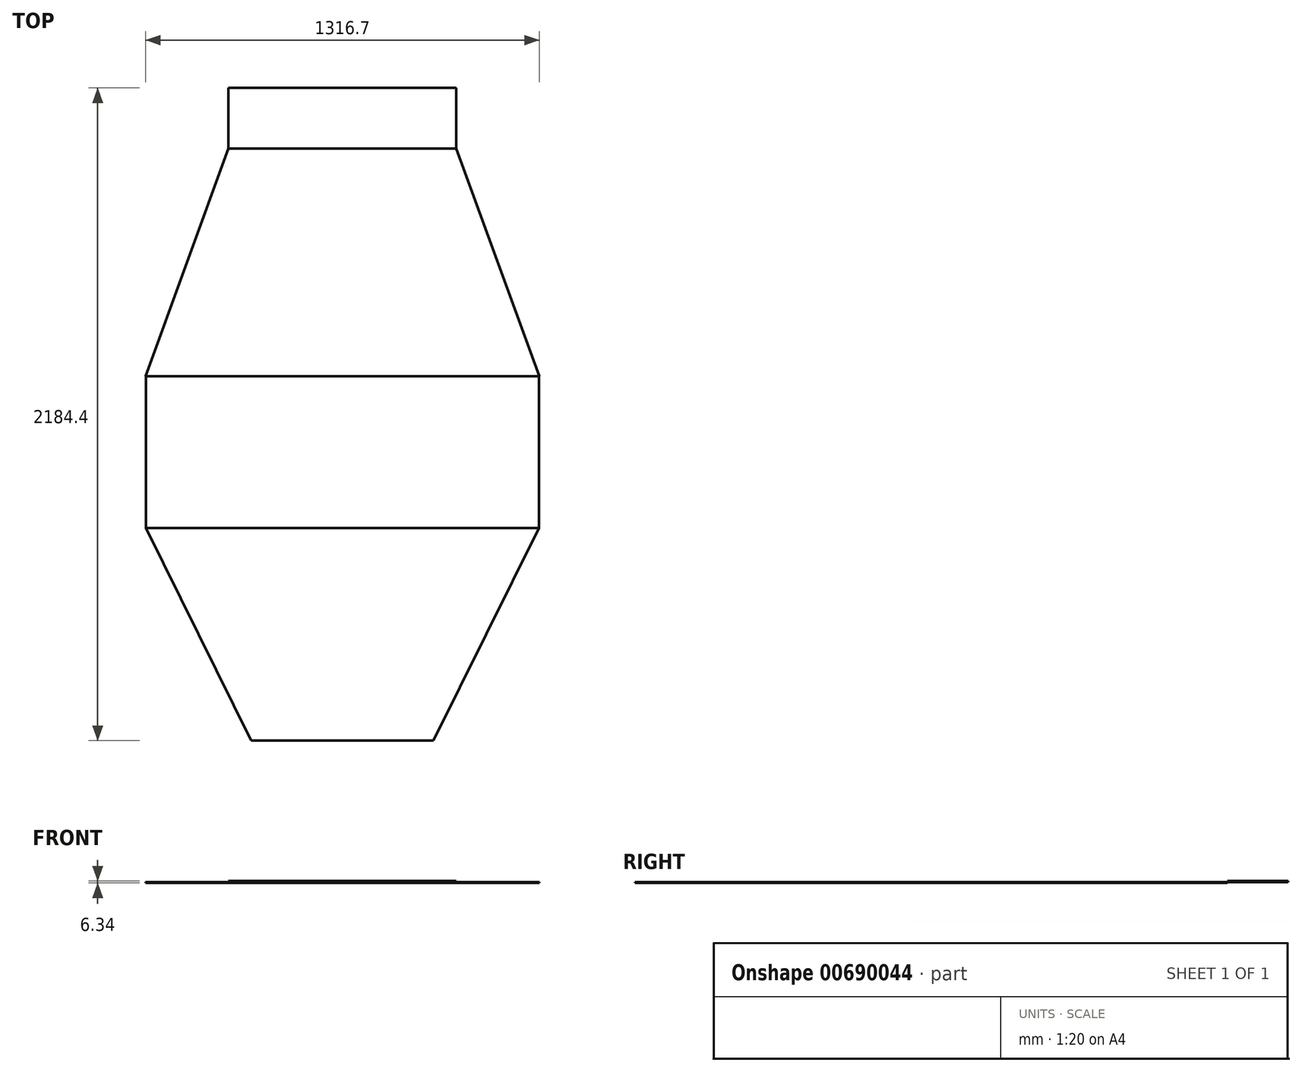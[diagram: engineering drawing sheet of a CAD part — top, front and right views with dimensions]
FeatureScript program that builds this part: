
annotation { "Feature Type Name" : "Feature", "Feature Type Description" : "" }
export const myFeature = defineFeature(function(context is Context, id is Id, definition is map)
    precondition{}
    {
        {
            var Q0;
            Q0=qCreatedBy(makeId("Top.planeOp"),FACE);
            var sketch = newSketch(context, id + "F0", { "sketchPlane" : qUnion([Q0])});
            skLineSegment(sketch, "E0.bottom", {"start": v(-381, 101.6) * mm, "end": v(381, 101.6) * mm});
            skLineSegment(sketch, "E0.top", {"start": v(-381, -101.6) * mm, "end": v(381, -101.6) * mm});
            skLineSegment(sketch, "E0.left", {"start": v(-381, 101.6) * mm, "end": v(-381, -101.6) * mm});
            skLineSegment(sketch, "E0.right", {"start": v(381, 101.6) * mm, "end": v(381, -101.6) * mm});
            skPoint(sketch, "E0.middle", {"position": v(0, 0) * mm});
            skSolve(sketch);
        }
        {
            var Q0;
            Q0 = qSketchRegion(id + "F0", true);
            extrude(context, id + "F1", {"entities" : qUnion([Q0]), "depth" : 3.17 * mm, "offsetDistance" : 25.4 * mm});
        }
        {
            var Q0;
            Q0=qCreatedBy(makeId("Top.planeOp"),FACE);
            var sketch = newSketch(context, id + "F2", { "sketchPlane" : qUnion([Q0])});
            skLineSegment(sketch, "E1", {"start": v(0, 0) * mm, "end": v(0, -101.6) * mm});
            skLineSegment(sketch, "E2", {"start": v(381, -101.6) * mm, "end": v(-381, -101.6) * mm});
            skLineSegment(sketch, "E3", {"start": v(-381, -101.6) * mm, "end": v(-658.35, -863.6) * mm});
            skLineSegment(sketch, "E4", {"start": v(381, -101.6) * mm, "end": v(658.35, -863.6) * mm});
            skLineSegment(sketch, "E5", {"start": v(0, -101.6) * mm, "end": v(0, -863.6) * mm});
            skLineSegment(sketch, "E6", {"start": v(-658.35, -863.6) * mm, "end": v(658.35, -863.6) * mm});
            skSolve(sketch);
        }
        {
            var Q0;
            Q0 = qSketchRegion(id + "F2", true);
            extrude(context, id + "F3", {"entities" : qUnion([Q0]), "operationType" : NewBodyOperationType.ADD, "oppositeDirection" : true, "depth" : 3.17 * mm, "offsetDistance" : 25.4 * mm});
        }
        {
            var Q0;
            Q0=qCreatedBy(makeId("Top.planeOp"),FACE);
            var sketch = newSketch(context, id + "F4", { "sketchPlane" : qUnion([Q0])});
            skLineSegment(sketch, "E7", {"start": v(0, 0) * mm, "end": v(0, -863.6) * mm});
            skLineSegment(sketch, "E8.bottom", {"start": v(-657.22, -863.6) * mm, "end": v(657.22, -863.6) * mm});
            skLineSegment(sketch, "E8.top", {"start": v(-657.22, -1371.6) * mm, "end": v(657.22, -1371.6) * mm});
            skLineSegment(sketch, "E8.left", {"start": v(-657.22, -863.6) * mm, "end": v(-657.22, -1371.6) * mm});
            skLineSegment(sketch, "E8.right", {"start": v(657.23, -863.6) * mm, "end": v(657.23, -1371.6) * mm});
            skSolve(sketch);
        }
        {
            var Q0;
            Q0 = qSketchRegion(id + "F4", true);
            extrude(context, id + "F5", {"entities" : qUnion([Q0]), "oppositeDirection" : true, "depth" : 3.17 * mm, "offsetDistance" : 25.4 * mm});
        }
        {
            var Q0;
            Q0=qCreatedBy(makeId("Top.planeOp"),FACE);
            var sketch = newSketch(context, id + "F6", { "sketchPlane" : qUnion([Q0])});
            skLineSegment(sketch, "E9", {"start": v(0, 0) * mm, "end": v(0, -1371.6) * mm});
            skLineSegment(sketch, "E10", {"start": v(-657.22, -1371.6) * mm, "end": v(657.23, -1371.6) * mm});
            skLineSegment(sketch, "E11", {"start": v(0, -1371.6) * mm, "end": v(0, -2082.8) * mm});
            skLineSegment(sketch, "E12", {"start": v(-304.8, -2082.8) * mm, "end": v(304.8, -2082.8) * mm});
            skLineSegment(sketch, "E13", {"start": v(-657.22, -1371.6) * mm, "end": v(-304.8, -2082.8) * mm});
            skLineSegment(sketch, "E14", {"start": v(304.8, -2082.8) * mm, "end": v(657.23, -1371.6) * mm});
            skSolve(sketch);
        }
        {
            var Q0;
            Q0 = qSketchRegion(id + "F6", true);
            extrude(context, id + "F7", {"entities" : qUnion([Q0]), "oppositeDirection" : true, "depth" : 3.17 * mm, "offsetDistance" : 25.4 * mm});
        }
    });
